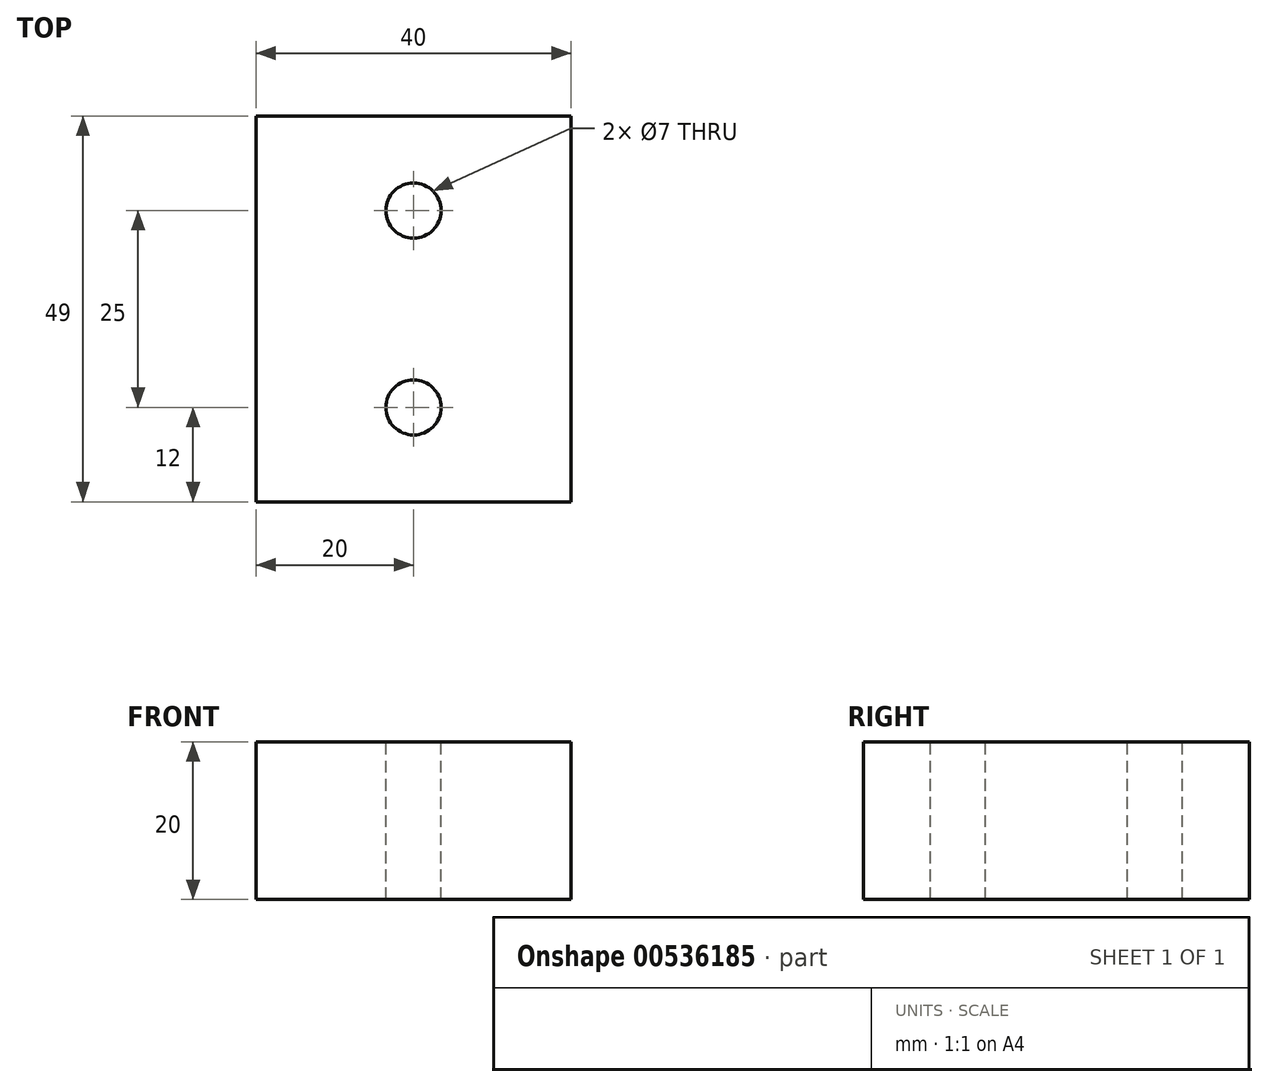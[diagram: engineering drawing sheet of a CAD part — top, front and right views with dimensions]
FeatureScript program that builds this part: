
annotation { "Feature Type Name" : "Feature", "Feature Type Description" : "" }
export const myFeature = defineFeature(function(context is Context, id is Id, definition is map)
    precondition{}
    {
        {
            var Q0;
            Q0=qCreatedBy(makeId("Top.planeOp"),FACE);
            var sketch = newSketch(context, id + "F0", { "sketchPlane" : qUnion([Q0])});
            skLineSegment(sketch, "E0.bottom", {"start": v(-20, 24.5) * mm, "end": v(20, 24.5) * mm});
            skLineSegment(sketch, "E0.top", {"start": v(-20, -24.5) * mm, "end": v(20, -24.5) * mm});
            skLineSegment(sketch, "E0.left", {"start": v(-20, 24.5) * mm, "end": v(-20, -24.5) * mm});
            skLineSegment(sketch, "E0.right", {"start": v(20, 24.5) * mm, "end": v(20, -24.5) * mm});
            skPoint(sketch, "E0.middle", {"position": v(0, 0) * mm});
            skSolve(sketch);
        }
        {
            var Q0;
            Q0 = qSketchRegion(id + "F0", true);
            extrude(context, id + "F1", {"entities" : qUnion([Q0]), "oppositeDirection" : true, "depth" : 20 * mm, "offsetDistance" : 25 * mm});
        }
        {
            var Q0;
            Q0=makeQuery(id+"F1.opExtrude","CAP_FACE",FACE,{"disambiguationData":[OSD([sQuery(id+"F0.wireOp",EDGE,"E0.bottom"),sQuery(id+"F0.wireOp",EDGE,"E0.top"),sQuery(id+"F0.wireOp",EDGE,"E0.left"),sQuery(id+"F0.wireOp",EDGE,"E0.right")])],"isStart":true});
            var sketch = newSketch(context, id + "F2", { "sketchPlane" : qUnion([Q0])});
            skPoint(sketch, "E1", {"position": v(0, -12.5) * mm});
            skPoint(sketch, "E2", {"position": v(0, 12.5) * mm});
            skSolve(sketch);
        }
        {
            var Q0;
            Q0=sQuery(id+"F2.wireOp",VERTEX,"E1");
            var Q1;
            Q1=sQuery(id+"F2.wireOp",VERTEX,"E2");
            var Q2;
            Q2=makeQuery(id+"F1.opExtrude","SWEPT_BODY",BODY,{"disambiguationData":[OSD([sQuery(id+"F0.wireOp",EDGE,"E0.bottom"),sQuery(id+"F0.wireOp",EDGE,"E0.top"),sQuery(id+"F0.wireOp",EDGE,"E0.left"),sQuery(id+"F0.wireOp",EDGE,"E0.right")])]});
            hole(context, id + "F3", {"style" : HoleStyle.SIMPLE, "endStyle" : HoleEndStyle.BLIND, "standardTappedOrClearance" : lookupTablePath({ "standard" : "ISO", "engagement" : "75%", "pitch" : "1 mm", "size" : "M8", "type" : "Tapped" }), "standardBlindInLast" : lookupTablePath({ "standard" : "ISO", "engagement" : "75%", "pitch" : "1 mm", "size" : "M8", "type" : "Tapped" }), "holeDiameter" : 7 * mm, "showTappedDepth" : true, "holeDepth" : 23 * mm, "isTappedThrough" : true, "tappedDepth" : 20 * mm, "tapClearance" : 3, "locations" : qUnion([Q0, Q1]), "scope" : qUnion([Q2]), "majorDiameter" : 8 * mm});
        }
    });
